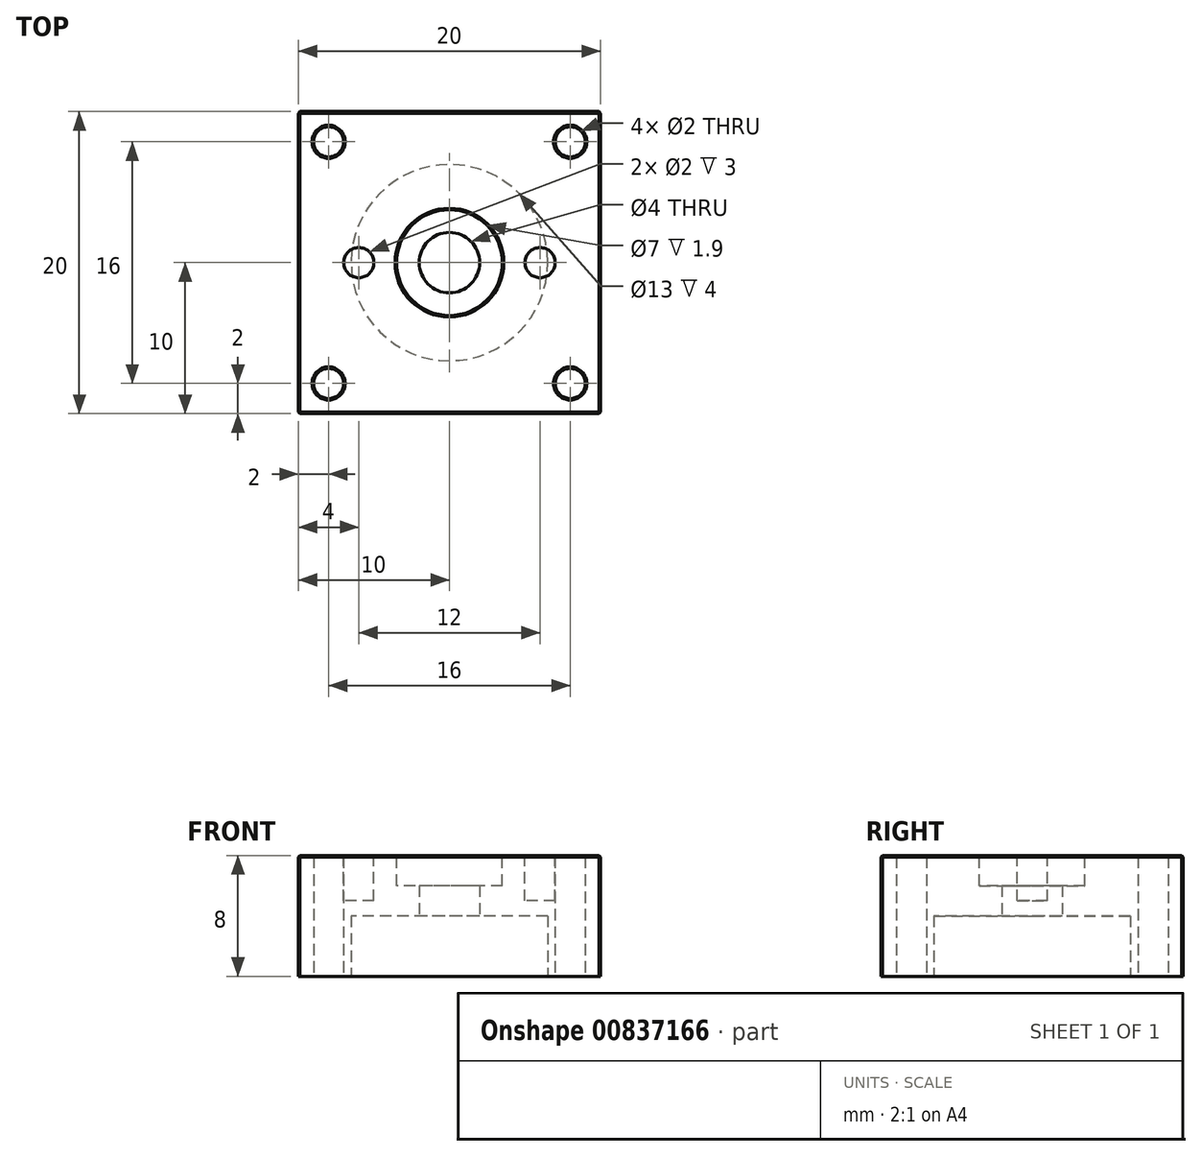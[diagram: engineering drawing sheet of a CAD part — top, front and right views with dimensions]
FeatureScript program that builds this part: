
annotation { "Feature Type Name" : "Feature", "Feature Type Description" : "" }
export const myFeature = defineFeature(function(context is Context, id is Id, definition is map)
    precondition{}
    {
        {
            var Q0;
            Q0=qCreatedBy(makeId("Top.planeOp"),FACE);
            var sketch = newSketch(context, id + "F0", { "sketchPlane" : qUnion([Q0])});
            skLineSegment(sketch, "E0.bottom", {"start": v(0, 0) * mm, "end": v(20, 0) * mm});
            skLineSegment(sketch, "E0.top", {"start": v(0, -20) * mm, "end": v(20, -20) * mm});
            skLineSegment(sketch, "E0.left", {"start": v(0, 0) * mm, "end": v(0, -20) * mm});
            skLineSegment(sketch, "E0.right", {"start": v(20, 0) * mm, "end": v(20, -20) * mm});
            skLineSegment(sketch, "E1", {"start": v(0, -10) * mm, "end": v(20, -10) * mm, "construction": true});
            skCircle(sketch, "E2", {"center": v(10, -10) * mm, "radius": 2 * mm});
            skCircle(sketch, "E3", {"center": v(10, -10) * mm, "radius": 5.5 * mm, "construction": true});
            skCircle(sketch, "E4", {"center": v(10, -10) * mm, "radius": 6.5 * mm});
            skCircle(sketch, "E5", {"center": v(10, -10) * mm, "radius": 7 * mm});
            skCircle(sketch, "E6", {"center": v(10, -10) * mm, "radius": 8.5 * mm});
            skCircle(sketch, "E7", {"center": v(10, -10) * mm, "radius": 3 * mm});
            skLineSegment(sketch, "E8", {"start": v(10, -10) * mm, "end": v(10, -5.75) * mm, "construction": true});
            skCircle(sketch, "E9", {"center": v(10, -5.75) * mm, "radius": 1.25 * mm});
            skCircle(sketch, "E10.1.0", {"center": v(5.75, -10) * mm, "radius": 1.25 * mm});
            skCircle(sketch, "E10.2.0", {"center": v(10, -14.25) * mm, "radius": 1.25 * mm});
            skCircle(sketch, "E10.3.0", {"center": v(14.25, -10) * mm, "radius": 1.25 * mm});
            skLineSegment(sketch, "E11", {"start": v(0, -2) * mm, "end": v(2, -2) * mm, "construction": true});
            skLineSegment(sketch, "E12", {"start": v(2, -2) * mm, "end": v(2, 0) * mm, "construction": true});
            skCircle(sketch, "E13", {"center": v(2, -2) * mm, "radius": 1 * mm});
            skCircle(sketch, "E14.1.0", {"center": v(2, -18) * mm, "radius": 1 * mm});
            skCircle(sketch, "E14.2.0", {"center": v(18, -18) * mm, "radius": 1 * mm});
            skCircle(sketch, "E14.3.0", {"center": v(18, -2) * mm, "radius": 1 * mm});
            skSolve(sketch);
        }
        {
            var Q0;
            Q0=makeQuery(id+"F0.imprint","IMPRINT",FACE,{"disambiguationData":[TD([[makeQuery(id+"F0.imprint","IMPRINT",EDGE,{"derivedFrom":sQuery(id+"F0.wireOp",EDGE,"E0.bottom")}),-1.0]])]});
            var Q1;
            Q1=makeQuery(id+"F0.imprint","IMPRINT",FACE,{"disambiguationData":[TD([[makeQuery(id+"F0.imprint","IMPRINT",EDGE,{"derivedFrom":sQuery(id+"F0.wireOp",EDGE,"E5")}),-1.0]])]});
            var Q2;
            Q2=makeQuery(id+"F0.imprint","IMPRINT",FACE,{"disambiguationData":[TD([[makeQuery(id+"F0.imprint","IMPRINT",EDGE,{"derivedFrom":sQuery(id+"F0.wireOp",EDGE,"E4")}),-1.0]])]});
            var Q3;
            Q3=makeQuery(id+"F0.imprint","IMPRINT",FACE,{"disambiguationData":[TD([[makeQuery(id+"F0.imprint","IMPRINT",EDGE,{"derivedFrom":sQuery(id+"F0.wireOp",EDGE,"E2")}),-1.0]])]});
            var Q4;
            Q4=makeQuery(id+"F0.imprint","IMPRINT",FACE,{"disambiguationData":[TD([[makeQuery(id+"F0.imprint","IMPRINT",EDGE,{"derivedFrom":sQuery(id+"F0.wireOp",EDGE,"E10.3.0")}),1.0]])]});
            var Q5;
            Q5=makeQuery(id+"F0.imprint","IMPRINT",FACE,{"disambiguationData":[TD([[makeQuery(id+"F0.imprint","IMPRINT",EDGE,{"derivedFrom":sQuery(id+"F0.wireOp",EDGE,"E9")}),1.0]])]});
            var Q6;
            Q6=makeQuery(id+"F0.imprint","IMPRINT",FACE,{"disambiguationData":[TD([[makeQuery(id+"F0.imprint","IMPRINT",EDGE,{"derivedFrom":sQuery(id+"F0.wireOp",EDGE,"E10.1.0")}),1.0]])]});
            var Q7;
            Q7=makeQuery(id+"F0.imprint","IMPRINT",FACE,{"disambiguationData":[TD([[makeQuery(id+"F0.imprint","IMPRINT",EDGE,{"derivedFrom":sQuery(id+"F0.wireOp",EDGE,"E10.2.0")}),1.0]])]});
            var Q8;
            Q8=makeQuery(id+"F0.imprint","IMPRINT",FACE,{"disambiguationData":[TD([[makeQuery(id+"F0.imprint","IMPRINT",EDGE,{"derivedFrom":sQuery(id+"F0.wireOp",EDGE,"E4")}),1.0]])]});
            extrude(context, id + "F1", {"entities" : qUnion([Q0, Q1, Q2, Q3, Q4, Q5, Q6, Q7, Q8]), "depth" : 8 * mm, "offsetDistance" : 25 * mm});
        }
        {
            var Q0;
            Q0=makeQuery(id+"F1.opExtrude","CAP_FACE",FACE,{"disambiguationData":[OSD([sQuery(id+"F0.wireOp",EDGE,"E0.bottom"),sQuery(id+"F0.wireOp",EDGE,"E0.top"),sQuery(id+"F0.wireOp",EDGE,"E0.left"),sQuery(id+"F0.wireOp",EDGE,"E0.right"),sQuery(id+"F0.wireOp",EDGE,"E2"),sQuery(id+"F0.wireOp",EDGE,"E13"),sQuery(id+"F0.wireOp",EDGE,"E14.1.0"),sQuery(id+"F0.wireOp",EDGE,"E14.2.0"),sQuery(id+"F0.wireOp",EDGE,"E14.3.0")])],"isStart":false});
            var sketch = newSketch(context, id + "F2", { "sketchPlane" : qUnion([Q0])});
            skCircle(sketch, "E15", {"center": v(0, -20) * mm, "radius": 6 * mm});
            skCircle(sketch, "E16.1.0", {"center": v(20, -20) * mm, "radius": 6 * mm});
            skCircle(sketch, "E16.2.0", {"center": v(20, 0) * mm, "radius": 6 * mm});
            skCircle(sketch, "E16.3.0", {"center": v(0, 0) * mm, "radius": 6 * mm});
            skPoint(sketch, "E16.center", {"position": v(10, -10) * mm});
            skCircle(sketch, "E17", {"center": v(10, -10) * mm, "radius": 8 * mm});
            skCircle(sketch, "E18", {"center": v(10, -10) * mm, "radius": 3.5 * mm});
            skSolve(sketch);
        }
        {
            var Q0;
            Q0=makeQuery(id+"F2.imprint","IMPRINT",FACE,{"disambiguationData":[TD([[makeQuery(id+"F2.imprint","IMPRINT",EDGE,{"derivedFrom":sQuery(id+"F2.wireOp",EDGE,"E18")}),1.0]])]});
            extrude(context, id + "F3", {"entities" : qUnion([Q0]), "operationType" : NewBodyOperationType.REMOVE, "oppositeDirection" : true, "depth" : 2 * mm, "offsetDistance" : 25 * mm});
        }
        {
            var Q0;
            Q0=makeQuery(id+"F1.opExtrude","CAP_FACE",FACE,{"disambiguationData":[OSD([sQuery(id+"F0.wireOp",EDGE,"E0.bottom"),sQuery(id+"F0.wireOp",EDGE,"E0.top"),sQuery(id+"F0.wireOp",EDGE,"E0.left"),sQuery(id+"F0.wireOp",EDGE,"E0.right"),sQuery(id+"F0.wireOp",EDGE,"E2"),sQuery(id+"F0.wireOp",EDGE,"E13"),sQuery(id+"F0.wireOp",EDGE,"E14.1.0"),sQuery(id+"F0.wireOp",EDGE,"E14.2.0"),sQuery(id+"F0.wireOp",EDGE,"E14.3.0")])],"isStart":false});
            var Q1;
            Q1=makeQuery(id+"F1.opExtrude","SWEPT_EDGE",EDGE,{"disambiguationData":[OSD([sQuery(id+"F0.wireOp",EDGE,"E0.top"),sQuery(id+"F0.wireOp",EDGE,"E0.right")])]});
            var Q2;
            Q2=makeQuery(id+"F1.opExtrude","SWEPT_EDGE",EDGE,{"disambiguationData":[OSD([sQuery(id+"F0.wireOp",EDGE,"E0.bottom"),sQuery(id+"F0.wireOp",EDGE,"E0.right")])]});
            var Q3;
            Q3=makeQuery(id+"F1.opExtrude","SWEPT_EDGE",EDGE,{"disambiguationData":[OSD([sQuery(id+"F0.wireOp",EDGE,"E0.top"),sQuery(id+"F0.wireOp",EDGE,"E0.left")])]});
            var Q4;
            Q4=makeQuery(id+"F1.opExtrude","SWEPT_EDGE",EDGE,{"disambiguationData":[OSD([sQuery(id+"F0.wireOp",EDGE,"E0.bottom"),sQuery(id+"F0.wireOp",EDGE,"E0.left")])]});
            var Q5;
            Q5=makeQuery(id+"FpLN0tjRa3f56pI_1.boolean.opBoolean","COPY",EDGE,{"derivedFrom":makeQuery(id+"FpLN0tjRa3f56pI_1.opExtrude","CAP_EDGE",EDGE,{"disambiguationData":[OSD([sQuery(id+"F0.wireOp",EDGE,"E2")])],"isStart":false})});
            var Q6;
            Q6=makeQuery(id+"FpLN0tjRa3f56pI_1.boolean.opBoolean","COPY",EDGE,{"derivedFrom":makeQuery(id+"FpLN0tjRa3f56pI_1.opExtrude","CAP_EDGE",EDGE,{"disambiguationData":[OSD([sQuery(id+"F0.wireOp",EDGE,"E7")])],"isStart":true})});
            var Q7;
            Q7=makeQuery(id+"F3.boolean.opBoolean","COPY",EDGE,{"derivedFrom":makeQuery(id+"F3.opExtrude","CAP_EDGE",EDGE,{"disambiguationData":[OSD([sQuery(id+"F0.wireOp",EDGE,"E2")])],"isStart":false})});
            chamfer(context, id + "F4", {"entities" : qUnion([Q0, Q1, Q2, Q3, Q4, Q5, Q6, Q7]), "width" : .1 * mm, "tangentPropagation" : true});
        }
        {
            var Q0;
            Q0=makeQuery(id+"F0.imprint","IMPRINT",FACE,{"disambiguationData":[TD([[makeQuery(id+"F0.imprint","IMPRINT",EDGE,{"derivedFrom":sQuery(id+"F0.wireOp",EDGE,"E4")}),1.0]])]});
            var Q1;
            Q1=makeQuery(id+"F0.imprint","IMPRINT",FACE,{"disambiguationData":[TD([[makeQuery(id+"F0.imprint","IMPRINT",EDGE,{"derivedFrom":sQuery(id+"F0.wireOp",EDGE,"E2")}),-1.0]])]});
            var Q2;
            Q2=makeQuery(id+"F0.imprint","IMPRINT",FACE,{"disambiguationData":[TD([[makeQuery(id+"F0.imprint","IMPRINT",EDGE,{"derivedFrom":sQuery(id+"F0.wireOp",EDGE,"E10.3.0")}),1.0]])]});
            var Q3;
            Q3=makeQuery(id+"F0.imprint","IMPRINT",FACE,{"disambiguationData":[TD([[makeQuery(id+"F0.imprint","IMPRINT",EDGE,{"derivedFrom":sQuery(id+"F0.wireOp",EDGE,"E10.2.0")}),1.0]])]});
            var Q4;
            Q4=makeQuery(id+"F0.imprint","IMPRINT",FACE,{"disambiguationData":[TD([[makeQuery(id+"F0.imprint","IMPRINT",EDGE,{"derivedFrom":sQuery(id+"F0.wireOp",EDGE,"E10.1.0")}),1.0]])]});
            var Q5;
            Q5=makeQuery(id+"F0.imprint","IMPRINT",FACE,{"disambiguationData":[TD([[makeQuery(id+"F0.imprint","IMPRINT",EDGE,{"derivedFrom":sQuery(id+"F0.wireOp",EDGE,"E9")}),1.0]])]});
            extrude(context, id + "F5", {"entities" : qUnion([Q0, Q1, Q2, Q3, Q4, Q5]), "operationType" : NewBodyOperationType.REMOVE, "depth" : 4 * mm, "offsetDistance" : 25 * mm});
        }
        {
            var Q0;
            Q0=makeQuery(id+"F1.opExtrude","CAP_FACE",FACE,{"disambiguationData":[OSD([sQuery(id+"F0.wireOp",EDGE,"E0.bottom"),sQuery(id+"F0.wireOp",EDGE,"E0.top"),sQuery(id+"F0.wireOp",EDGE,"E0.left"),sQuery(id+"F0.wireOp",EDGE,"E0.right"),sQuery(id+"F0.wireOp",EDGE,"E2"),sQuery(id+"F0.wireOp",EDGE,"E13"),sQuery(id+"F0.wireOp",EDGE,"E14.1.0"),sQuery(id+"F0.wireOp",EDGE,"E14.2.0"),sQuery(id+"F0.wireOp",EDGE,"E14.3.0")])],"isStart":false});
            var sketch = newSketch(context, id + "F6", { "sketchPlane" : qUnion([Q0])});
            skLineSegment(sketch, "E19", {"start": v(0.1, -10) * mm, "end": v(19.9, -10) * mm, "construction": true});
            skCircle(sketch, "E20", {"center": v(4, -10) * mm, "radius": 1 * mm});
            skCircle(sketch, "E21", {"center": v(16, -10) * mm, "radius": 1 * mm});
            skSolve(sketch);
        }
        {
            var Q0;
            Q0=makeQuery(id+"F6.imprint","IMPRINT",FACE,{"disambiguationData":[TD([[makeQuery(id+"F6.imprint","IMPRINT",EDGE,{"derivedFrom":sQuery(id+"F6.wireOp",EDGE,"E20")}),1.0]])]});
            var Q1;
            Q1=makeQuery(id+"F6.imprint","IMPRINT",FACE,{"disambiguationData":[TD([[makeQuery(id+"F6.imprint","IMPRINT",EDGE,{"derivedFrom":sQuery(id+"F6.wireOp",EDGE,"E21")}),1.0]])]});
            extrude(context, id + "F7", {"entities" : qUnion([Q0, Q1]), "operationType" : NewBodyOperationType.REMOVE, "oppositeDirection" : true, "depth" : 3 * mm, "offsetDistance" : 25 * mm});
        }
    });
